# Revit family: TD92_SIS046_BRA010_RVT20_R00
name_source: partatom
category: Mobiliário
units: mm (PartAtom-declared; Revit-internal decimal feet)

## family parameters
Com base no plano de trabalho = Não
Compartilhado = Não
Corte com vazios quando carregada = Não
Número OmniClass = 23.40.20.00
Ponto de cálculo do ambiente = Não
Sempre na vertical = Sim
Título OmniClass = General Furniture and Specialties

## types (1)
- TD92_SIS046_BRA010_RVT20_R00
    Descrição = Para criar um ambiente ainda mais despojado, criativo e descontraído, a Cadeira Tramontina Sissi Amarela sem Braços Encosto Fechado em Polipropileno e Fibra de Vidro da linha Summa é a escolha perfeita! Seu design diferenciado com encosto fechado mostra robustez sem esconder a sutileza das suas linhas. A Sissi é uma cadeira monobloco, empilhável, leve e resistente, sendo produzida com tecnologia de ponta de alta qualidade. Sua principal matéria-prima é fibra de vidro e aditivos, portanto é altamente durável. Deve-se evitar a exposição prolongada ao sol. Resistente a uma carga estática de até 182 kg. É certificada pelo Inmetro.
    Elevação padrão = 0 mm  [stored 0 ft]
    Fabricante = Tramontina Delta S/A
    Modelo = Cadeira Tramontina Sissi Amarela sem Braços Encosto Fechado em Polipropileno e Fibra de Vidro
    Nota-chave = 92046000
    URL = https://www.tramontinastore.com

note: [stored X ft] marks values corroborated as IEEE doubles in the binary element streams (Revit-internal decimal feet)
